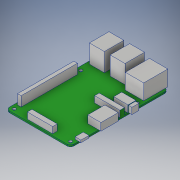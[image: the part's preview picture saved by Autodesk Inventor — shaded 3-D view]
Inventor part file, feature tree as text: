
AUTODESK INVENTOR PART (.ipt)
format: ipt  version: 2017 (Build 210142000, 142)  size: 381,952 bytes
history: native  units: in
note: dims shown in document units (in); Inventor stores cm internally (conversion verified against a paired STEP export)
features: projected_geometry x11, extrude x10, sketch x10, fillet x1
ambient origin geometry x8: Origin, YZ Plane, XZ Plane, XY Plane, X Axis, Y Axis, Z Axis, Center Point
bodies: Solid1 (feature_tree)
feature tree (32):
  extrude  "Extrusion1"  Depth=2.2047in
  extrude  "Extrusion2"  Depth=0.0563in
  fillet  "Fillet1"  Radius=0.1083in
  extrude  "Extrusion3"  Depth=0.1083in
  extrude  "Extrusion4"  Depth=2.2835in
  extrude  "Extrusion5"  Depth=0.1378in
  extrude  "Extrusion6"  Depth=0.1181in
  extrude  "Extrusion7"  Depth=0.0787in
  extrude  "Extrusion8"  Depth=0.5118in
  extrude  "Extrusion9"  Depth=0.6693in
  extrude  "Extrusion10"  Depth=0.0787in
  sketch  "Sketch1"  dims[d0=3.3465in d1=2.2047in]
  sketch  "Sketch2"  dims[d2=0.0563in d3=0.0in d4=0.1083in d5=0.1083in]
  projected_geometry  "Projected Loop1"
  sketch  "Sketch3"  dims[d6=0.1083in d7=0.1083in]
  projected_geometry  "Projected Loop2"
  sketch  "Sketch4"  dims[d8=1.9291in d9=2.2835in]
  projected_geometry  "Projected Loop3"
  projected_geometry  "Projected Loop4"
  sketch  "Sketch5"  dims[d10=0.1378in d11=0.1378in]
  projected_geometry  "Projected Loop5"
  sketch  "Sketch6"  dims[d12=0.0563in d13=0.0in d14=0.1181in]
  projected_geometry  "Projected Loop6"
  sketch  "Sketch7"  dims[d15=0.0787in d16=1.1417in]
  projected_geometry  "Projected Loop7"
  projected_geometry  "Projected Loop8"
  sketch  "Sketch8"  dims[d17=1.8504in d18=0.5118in]
  projected_geometry  "Projected Loop9"
  sketch  "Sketch9"  dims[d19=0.5118in d20=0.6693in]
  projected_geometry  "Projected Loop10"
  sketch  "Sketch10"  dims[d21=0.6299in d22=0.0in d23=0.4035in d24=0.8268in d25=0.6299in d26=0.5315in d27=0.0in d28=0.124in d29=1.9291in d31=1.1417in d32=0.3346in d33=0.0in d34=0.0787in d35=0.4528in d36=0.5906in d37=1.2598in d38=0.2559in d39=0.0in d40=0.8661in d41=0.8661in d42=0.1575in d43=0.1575in d44=1.1024in d45=0.5118in d46=0.2165in d47=0.0in d48=0.2756in d49=0.2362in d50=0.4882in d51=0.1181in d52=2.1063in d53=0.2362in d54=0.0in d55=0.0197in d56=0.0in d57=0.0787in d58=0.4173in d59=0.1969in d60=0.2756in d61=0.0787in d62=0.0in]
  projected_geometry  "Projected Loop11"
